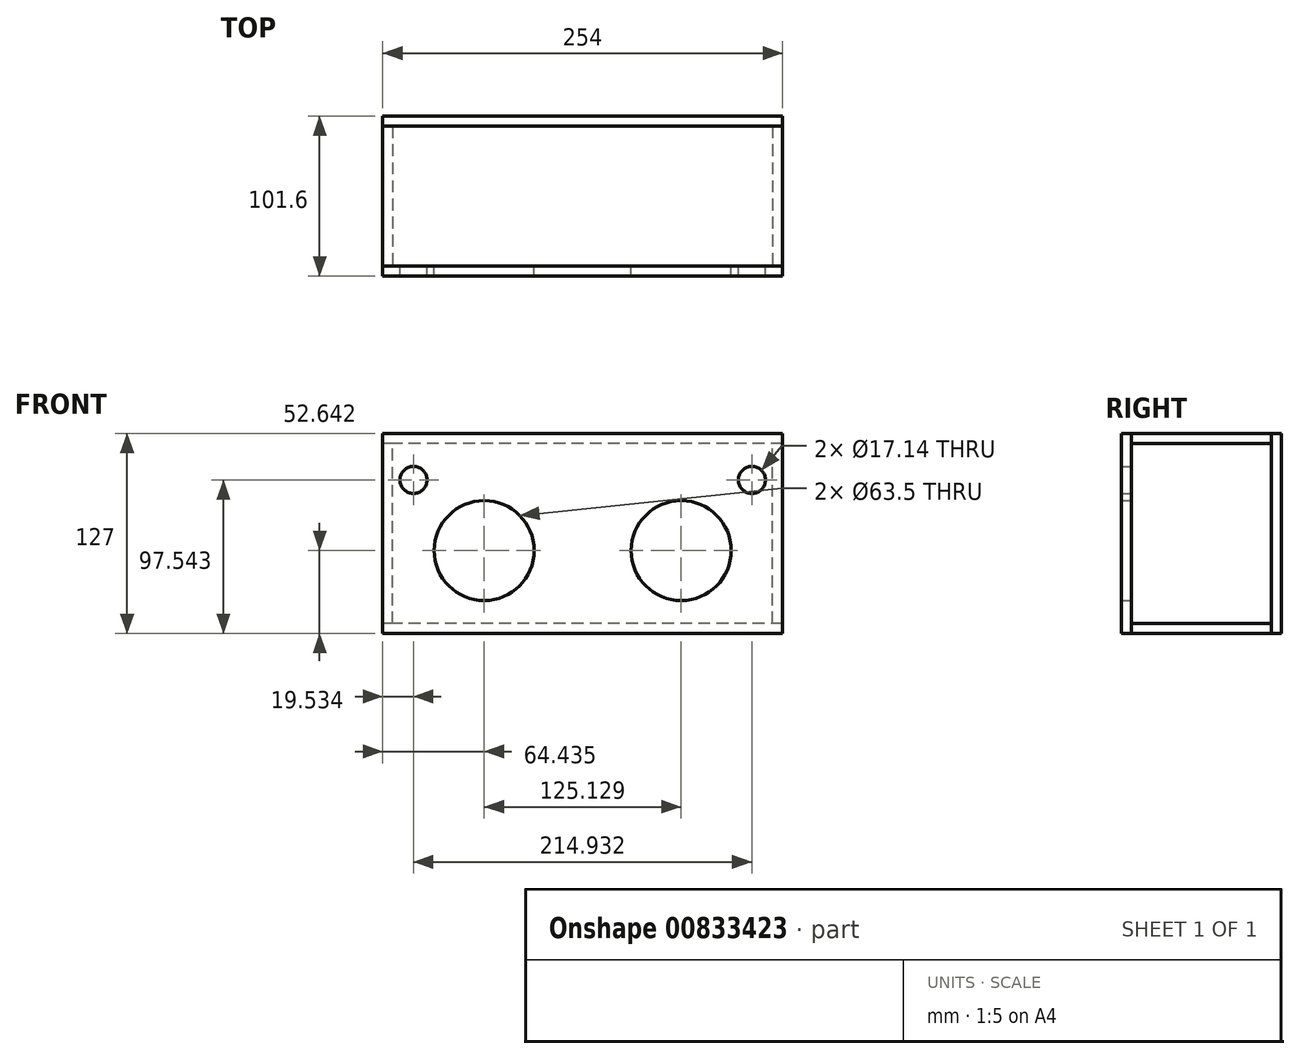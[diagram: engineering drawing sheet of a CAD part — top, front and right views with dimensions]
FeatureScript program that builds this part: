
annotation { "Feature Type Name" : "Feature", "Feature Type Description" : "" }
export const myFeature = defineFeature(function(context is Context, id is Id, definition is map)
    precondition{}
    {
        {
            var Q0;
            Q0=qCreatedBy(makeId("Front.planeOp"),FACE);
            var sketch = newSketch(context, id + "F0", { "sketchPlane" : qUnion([Q0])});
            skLineSegment(sketch, "E0.bottom", {"start": v(127, 63.5) * mm, "end": v(-127, 63.5) * mm});
            skLineSegment(sketch, "E0.top", {"start": v(127, -63.5) * mm, "end": v(-127, -63.5) * mm});
            skLineSegment(sketch, "E0.left", {"start": v(127, 63.5) * mm, "end": v(127, -63.5) * mm});
            skLineSegment(sketch, "E0.right", {"start": v(-127, 63.5) * mm, "end": v(-127, -63.5) * mm});
            skPoint(sketch, "E0.middle", {"position": v(0, 0) * mm});
            skCircle(sketch, "E1", {"center": v(62.56, -10.86) * mm, "radius": 31.75 * mm});
            skCircle(sketch, "E2", {"center": v(-62.56, -10.86) * mm, "radius": 31.75 * mm});
            skCircle(sketch, "E3", {"center": v(-107.47, 34.04) * mm, "radius": 8.57 * mm});
            skCircle(sketch, "E4", {"center": v(107.47, 34.04) * mm, "radius": 8.57 * mm});
            skLineSegment(sketch, "E5", {"start": v(-62.56, -10.86) * mm, "end": v(62.56, -10.86) * mm, "construction": true});
            skCircle(sketch, "E6", {"center": v(85.02, 11.6) * mm, "radius": 31.75 * mm, "construction": true});
            skCircle(sketch, "E7", {"center": v(-85.02, 11.6) * mm, "radius": 31.75 * mm, "construction": true});
            skCircle(sketch, "E8", {"center": v(0, 0) * mm, "radius": 63.5 * mm, "construction": true});
            skLineSegment(sketch, "E9", {"start": v(-62.56, -10.86) * mm, "end": v(-107.47, 34.04) * mm, "construction": true});
            skLineSegment(sketch, "E10", {"start": v(107.47, 34.04) * mm, "end": v(62.56, -10.86) * mm, "construction": true});
            skSolve(sketch);
        }
        {
            var Q0;
            Q0=makeQuery(id+"F0.imprint","IMPRINT",FACE,{"disambiguationData":[TD([[makeQuery(id+"F0.imprint","IMPRINT",EDGE,{"derivedFrom":sQuery(id+"F0.wireOp",EDGE,"E0.bottom")}),1.0]])]});
            extrude(context, id + "F1", {"entities" : qUnion([Q0]), "depth" : 6.35 * mm, "offsetDistance" : 25.4 * mm});
        }
        {
            var Q0;
            Q0=makeQuery(id+"F1.opExtrude","SWEPT_FACE",FACE,{"disambiguationData":[OSD([sQuery(id+"F0.wireOp",EDGE,"E0.top")])]});
            var sketch = newSketch(context, id + "F2", { "sketchPlane" : qUnion([Q0])});
            skLineSegment(sketch, "E11.bottom", {"start": v(-127, 6.35) * mm, "end": v(127, 6.35) * mm});
            skLineSegment(sketch, "E11.left", {"start": v(-127, 6.35) * mm, "end": v(-127, -88.9) * mm});
            skLineSegment(sketch, "E12", {"start": v(-127, 0) * mm, "end": v(127, 0) * mm});
            skLineSegment(sketch, "E13", {"start": v(127, 6.35) * mm, "end": v(127, -88.9) * mm});
            skLineSegment(sketch, "E14", {"start": v(127, -88.9) * mm, "end": v(-127, -88.9) * mm});
            skSolve(sketch);
        }
        {
            var Q0;
            {var subQ0=sQuery(id+"F2.wireOp",EDGE,"E12");Q0=makeQuery(id+"F2.imprint","IMPRINT",FACE,{"disambiguationData":[TD([[makeQuery(id+"F2.imprint","IMPRINT",EDGE,{"derivedFrom":subQ0}),1.0]])]});}
            extrude(context, id + "F3", {"entities" : qUnion([Q0]), "oppositeDirection" : true, "depth" : 6.35 * mm, "offsetDistance" : 25.4 * mm});
        }
        {
            var Q0;
            Q0=makeQuery(id+"F3.opExtrude","CAP_FACE",FACE,{"disambiguationData":[OSD([sQuery(id+"F2.wireOp",EDGE,"E11.left"),sQuery(id+"F2.wireOp",EDGE,"E12"),sQuery(id+"F2.wireOp",EDGE,"E13"),sQuery(id+"F2.wireOp",EDGE,"E14")])],"isStart":true});
            var sketch = newSketch(context, id + "F4", { "sketchPlane" : qUnion([Q0])});
            skLineSegment(sketch, "E15.bottom", {"start": v(-127, -88.9) * mm, "end": v(127, -88.9) * mm});
            skLineSegment(sketch, "E15.top", {"start": v(-127, -95.25) * mm, "end": v(127, -95.25) * mm});
            skLineSegment(sketch, "E15.left", {"start": v(-127, -88.9) * mm, "end": v(-127, -95.25) * mm});
            skLineSegment(sketch, "E15.right", {"start": v(127, -88.9) * mm, "end": v(127, -95.25) * mm});
            skSolve(sketch);
        }
        {
            var Q0;
            Q0 = qSketchRegion(id + "F4", true);
            extrude(context, id + "F5", {"entities" : qUnion([Q0]), "oppositeDirection" : true, "depth" : 127 * mm, "offsetDistance" : 25.4 * mm});
        }
        {
            var Q0;
            Q0=makeQuery(id+"F5.opExtrude","SWEPT_FACE",FACE,{"disambiguationData":[OSD([sQuery(id+"F4.wireOp",EDGE,"E15.bottom")])]});
            var sketch = newSketch(context, id + "F6", { "sketchPlane" : qUnion([Q0])});
            skLineSegment(sketch, "E16.bottom", {"start": v(127, 63.5) * mm, "end": v(-127, 63.5) * mm});
            skLineSegment(sketch, "E16.top", {"start": v(127, 57.15) * mm, "end": v(-127, 57.15) * mm});
            skLineSegment(sketch, "E16.left", {"start": v(127, 63.5) * mm, "end": v(127, 57.15) * mm});
            skLineSegment(sketch, "E16.right", {"start": v(-127, 63.5) * mm, "end": v(-127, 57.15) * mm});
            skSolve(sketch);
        }
        {
            var Q0;
            Q0 = qSketchRegion(id + "F6", true);
            extrude(context, id + "F7", {"entities" : qUnion([Q0]), "endBound" : BoundingType.UP_TO_NEXT, "depth" : 25.4 * mm, "offsetDistance" : 25.4 * mm});
        }
        {
            var Q0;
            Q0=makeQuery(id+"F7.opExtrude","SWEPT_FACE",FACE,{"disambiguationData":[OSD([sQuery(id+"F6.wireOp",EDGE,"E16.top")])]});
            var sketch = newSketch(context, id + "F8", { "sketchPlane" : qUnion([Q0])});
            skLineSegment(sketch, "E17.bottom", {"start": v(-127, -88.9) * mm, "end": v(-120.65, -88.9) * mm});
            skLineSegment(sketch, "E17.top", {"start": v(-127, 0) * mm, "end": v(-120.65, 0) * mm});
            skLineSegment(sketch, "E17.left", {"start": v(-127, -88.9) * mm, "end": v(-127, 0) * mm});
            skLineSegment(sketch, "E17.right", {"start": v(-120.65, -88.9) * mm, "end": v(-120.65, 0) * mm});
            skLineSegment(sketch, "E18.bottom", {"start": v(127, -88.9) * mm, "end": v(120.65, -88.9) * mm});
            skLineSegment(sketch, "E18.top", {"start": v(127, 0) * mm, "end": v(120.65, 0) * mm});
            skLineSegment(sketch, "E18.left", {"start": v(127, -88.9) * mm, "end": v(127, 0) * mm});
            skLineSegment(sketch, "E18.right", {"start": v(120.65, -88.9) * mm, "end": v(120.65, 0) * mm});
            skSolve(sketch);
        }
        {
            var Q0;
            Q0 = qSketchRegion(id + "F8", true);
            extrude(context, id + "F9", {"entities" : qUnion([Q0]), "endBound" : BoundingType.UP_TO_NEXT, "depth" : 25.4 * mm, "offsetDistance" : 25.4 * mm});
        }
    });
